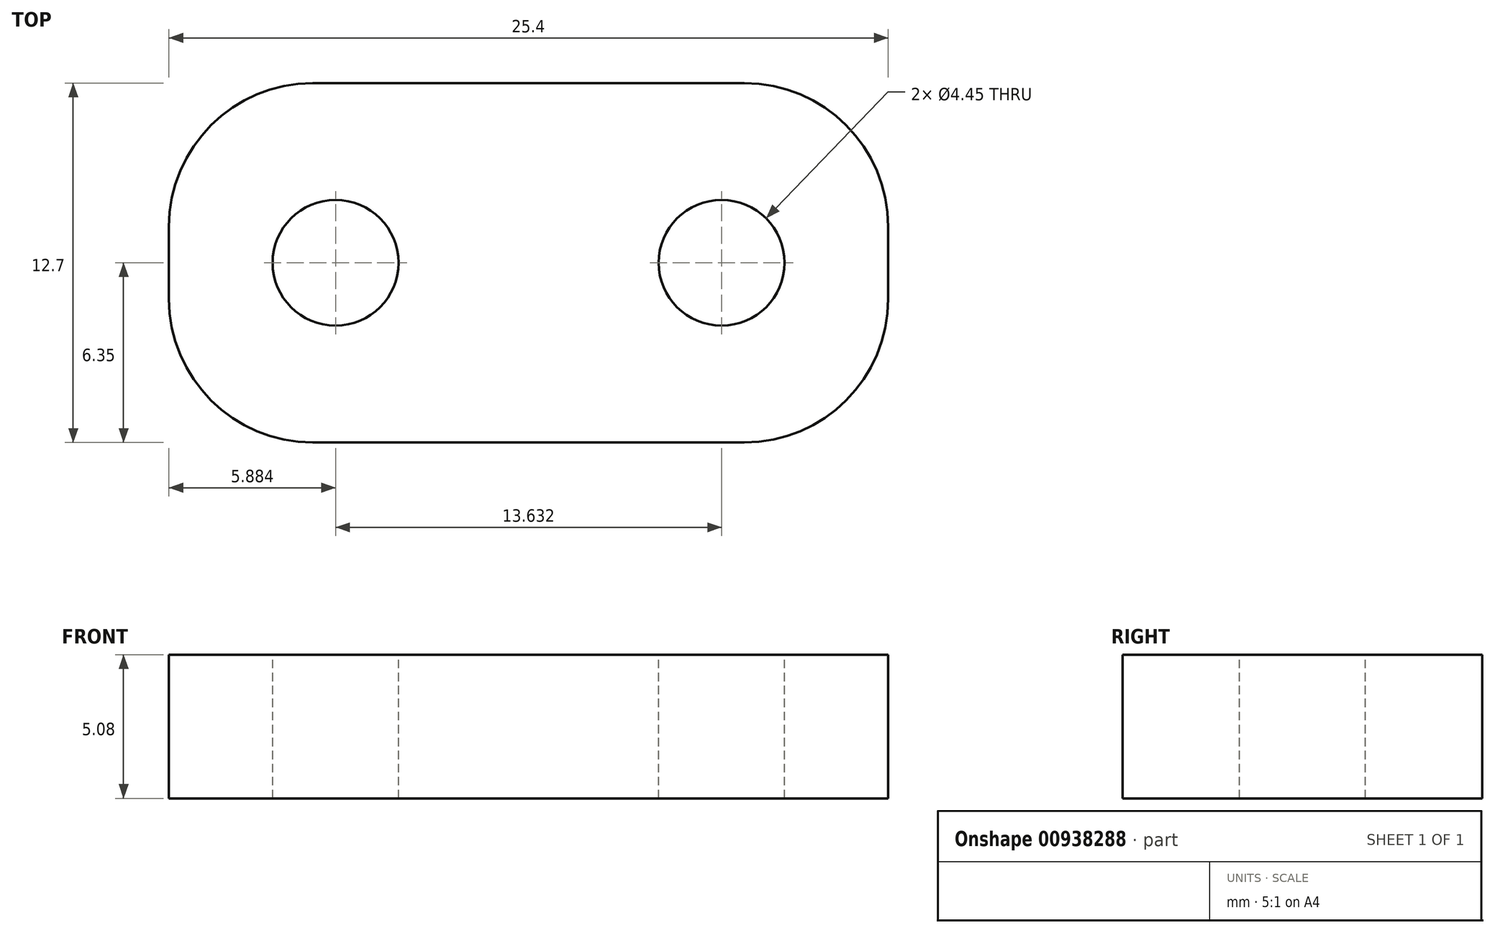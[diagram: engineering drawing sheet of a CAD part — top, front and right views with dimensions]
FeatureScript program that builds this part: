
annotation { "Feature Type Name" : "Feature", "Feature Type Description" : "" }
export const myFeature = defineFeature(function(context is Context, id is Id, definition is map)
    precondition{}
    {
        {
            var Q0;
            Q0=qCreatedBy(makeId("Top.planeOp"),FACE);
            var sketch = newSketch(context, id + "F0", { "sketchPlane" : qUnion([Q0])});
            skLineSegment(sketch, "E0.bottom", {"start": v(-12.7, 6.35) * mm, "end": v(12.7, 6.35) * mm});
            skLineSegment(sketch, "E0.top", {"start": v(-12.7, -6.35) * mm, "end": v(12.7, -6.35) * mm});
            skLineSegment(sketch, "E0.left", {"start": v(-12.7, 6.35) * mm, "end": v(-12.7, -6.35) * mm});
            skLineSegment(sketch, "E0.right", {"start": v(12.7, 6.35) * mm, "end": v(12.7, -6.35) * mm});
            skPoint(sketch, "E0.middle", {"position": v(0, 0) * mm});
            skCircle(sketch, "E1", {"center": v(6.82, 0) * mm, "radius": 2.22 * mm});
            skCircle(sketch, "E2.MirrorC", {"center": v(-6.82, 0) * mm, "radius": 2.22 * mm});
            skSolve(sketch);
        }
        {
            var Q0;
            Q0=makeQuery(id+"F0.imprint","IMPRINT",FACE,{"disambiguationData":[TD([[makeQuery(id+"F0.imprint","IMPRINT",EDGE,{"derivedFrom":sQuery(id+"F0.wireOp",EDGE,"E0.bottom")}),-1.0]])]});
            extrude(context, id + "F1", {"entities" : qUnion([Q0]), "oppositeDirection" : true, "depth" : 5.08 * mm, "offsetDistance" : 25.4 * mm});
        }
        {
            var Q0;
            Q0=makeQuery(id+"F1.opExtrude","SWEPT_EDGE",EDGE,{"disambiguationData":[OSD([sQuery(id+"F0.wireOp",EDGE,"E0.bottom"),sQuery(id+"F0.wireOp",EDGE,"E0.right")])]});
            var Q1;
            Q1=makeQuery(id+"F1.opExtrude","SWEPT_EDGE",EDGE,{"disambiguationData":[OSD([sQuery(id+"F0.wireOp",EDGE,"E0.top"),sQuery(id+"F0.wireOp",EDGE,"E0.right")])]});
            var Q2;
            Q2=makeQuery(id+"F1.opExtrude","SWEPT_EDGE",EDGE,{"disambiguationData":[OSD([sQuery(id+"F0.wireOp",EDGE,"E0.bottom"),sQuery(id+"F0.wireOp",EDGE,"E0.left")])]});
            var Q3;
            Q3=makeQuery(id+"F1.opExtrude","SWEPT_EDGE",EDGE,{"disambiguationData":[OSD([sQuery(id+"F0.wireOp",EDGE,"E0.top"),sQuery(id+"F0.wireOp",EDGE,"E0.left")])]});
            fillet(context, id + "F2", {"entities" : qUnion([Q0, Q1, Q2, Q3]), "radius" : 5.08 * mm, "tangentPropagation" : true, "allowEdgeOverflow" : false});
        }
    });
